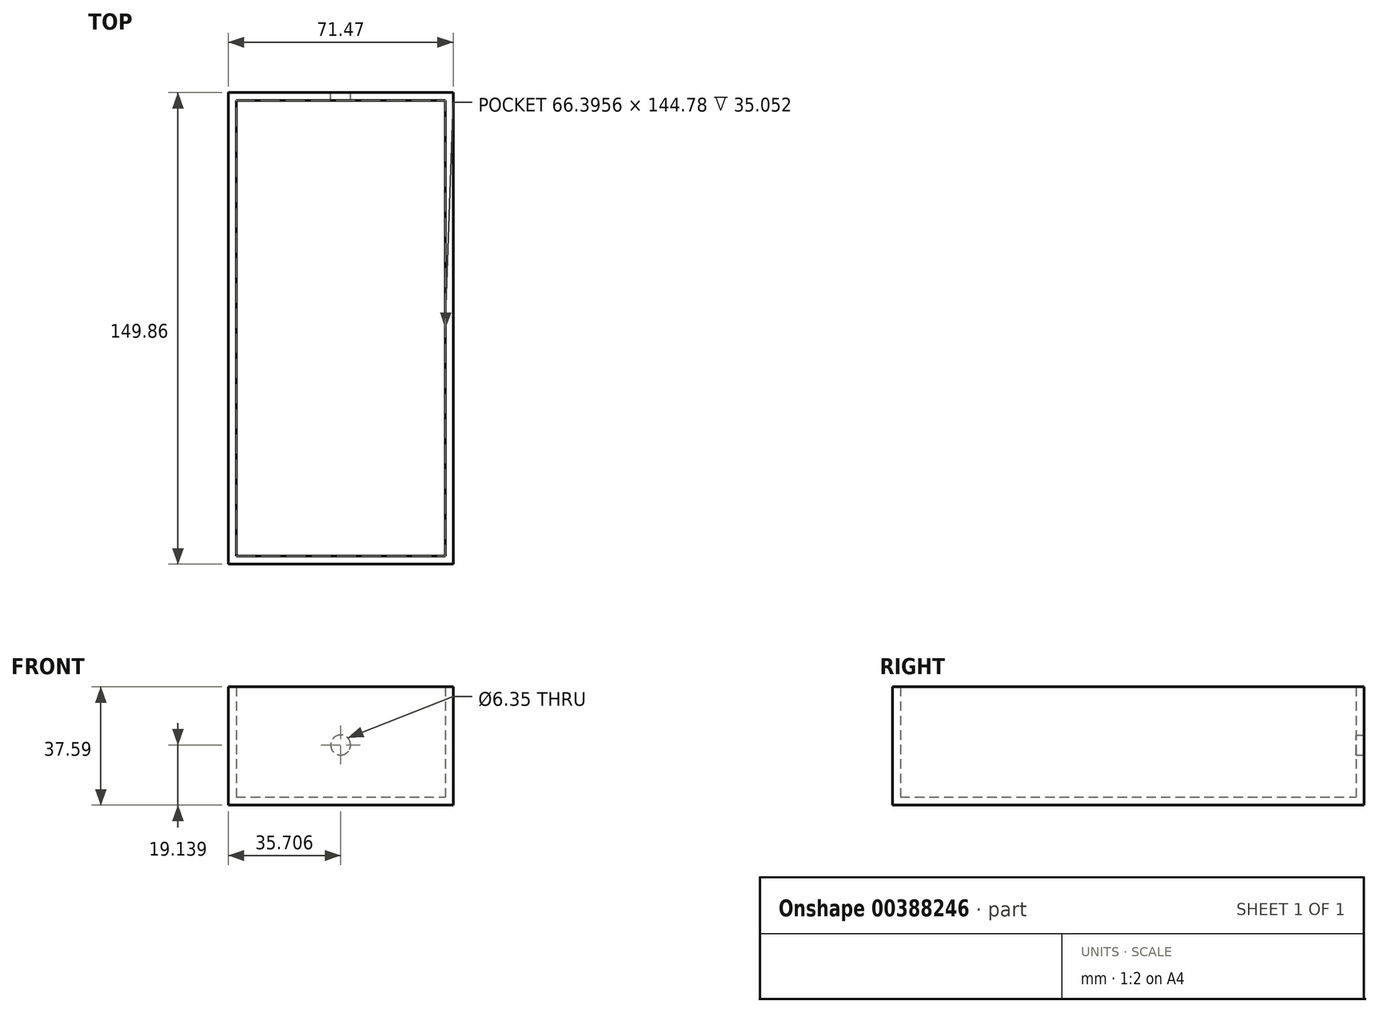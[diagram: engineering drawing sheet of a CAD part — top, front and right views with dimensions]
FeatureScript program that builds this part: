
annotation { "Feature Type Name" : "Feature", "Feature Type Description" : "" }
export const myFeature = defineFeature(function(context is Context, id is Id, definition is map)
    precondition{}
    {
        {
            var Q0;
            Q0=qCreatedBy(makeId("Front.planeOp"),FACE);
            var sketch = newSketch(context, id + "F0", { "sketchPlane" : qUnion([Q0])});
            skLineSegment(sketch, "E0.bottom", {"start": v(-39.16, 37.6) * mm, "end": v(32.31, 37.6) * mm});
            skLineSegment(sketch, "E0.top", {"start": v(-39.16, 0) * mm, "end": v(32.31, 0) * mm});
            skLineSegment(sketch, "E0.left", {"start": v(-39.16, 37.6) * mm, "end": v(-39.16, 0) * mm});
            skLineSegment(sketch, "E0.right", {"start": v(32.31, 37.6) * mm, "end": v(32.31, 0) * mm});
            skSolve(sketch);
        }
        {
            var Q0;
            Q0=makeQuery(id+"F0.imprint","IMPRINT",FACE,{"disambiguationData":[TD([[makeQuery(id+"F0.imprint","IMPRINT",EDGE,{"derivedFrom":sQuery(id+"F0.wireOp",EDGE,"E0.bottom")}),-1.0]])]});
            extrude(context, id + "F1", {"entities" : qUnion([Q0]), "depth" : 149.86 * mm});
        }
        {
            var Q0;
            Q0=makeQuery(id+"F1.opExtrude","SWEPT_FACE",FACE,{"disambiguationData":[OSD([sQuery(id+"F0.wireOp",EDGE,"E0.bottom")])]});
            shell(context, id + "F2", {"entities" : qUnion([Q0]), "thickness" : 2.54 * mm});
        }
        {
            var Q0;
            Q0=qCreatedBy(makeId("Front.planeOp"),FACE);
            var sketch = newSketch(context, id + "F3", { "sketchPlane" : qUnion([Q0])});
            skPoint(sketch, "E1", {"position": v(-3.45, 19.14) * mm});
            skSolve(sketch);
        }
        {
            var Q0;
            Q0=sQuery(id+"F3.wireOp",VERTEX,"E1");
            var Q1;
            Q1=makeQuery(id+"F1.opExtrude","SWEPT_BODY",BODY,{"disambiguationData":[OSD([sQuery(id+"F0.wireOp",EDGE,"E0.bottom"),sQuery(id+"F0.wireOp",EDGE,"E0.top"),sQuery(id+"F0.wireOp",EDGE,"E0.left"),sQuery(id+"F0.wireOp",EDGE,"E0.right")])]});
            hole(context, id + "F4", {"style" : HoleStyle.SIMPLE, "endStyle" : HoleEndStyle.BLIND, "oppositeDirection" : true, "holeDiameter" : 6.35 * mm, "holeDepth" : 25.4 * mm, "isTappedThrough" : true, "tappedDepth" : 12.7 * mm, "tapClearance" : 3, "locations" : qUnion([Q0]), "scope" : qUnion([Q1])});
        }
    });
